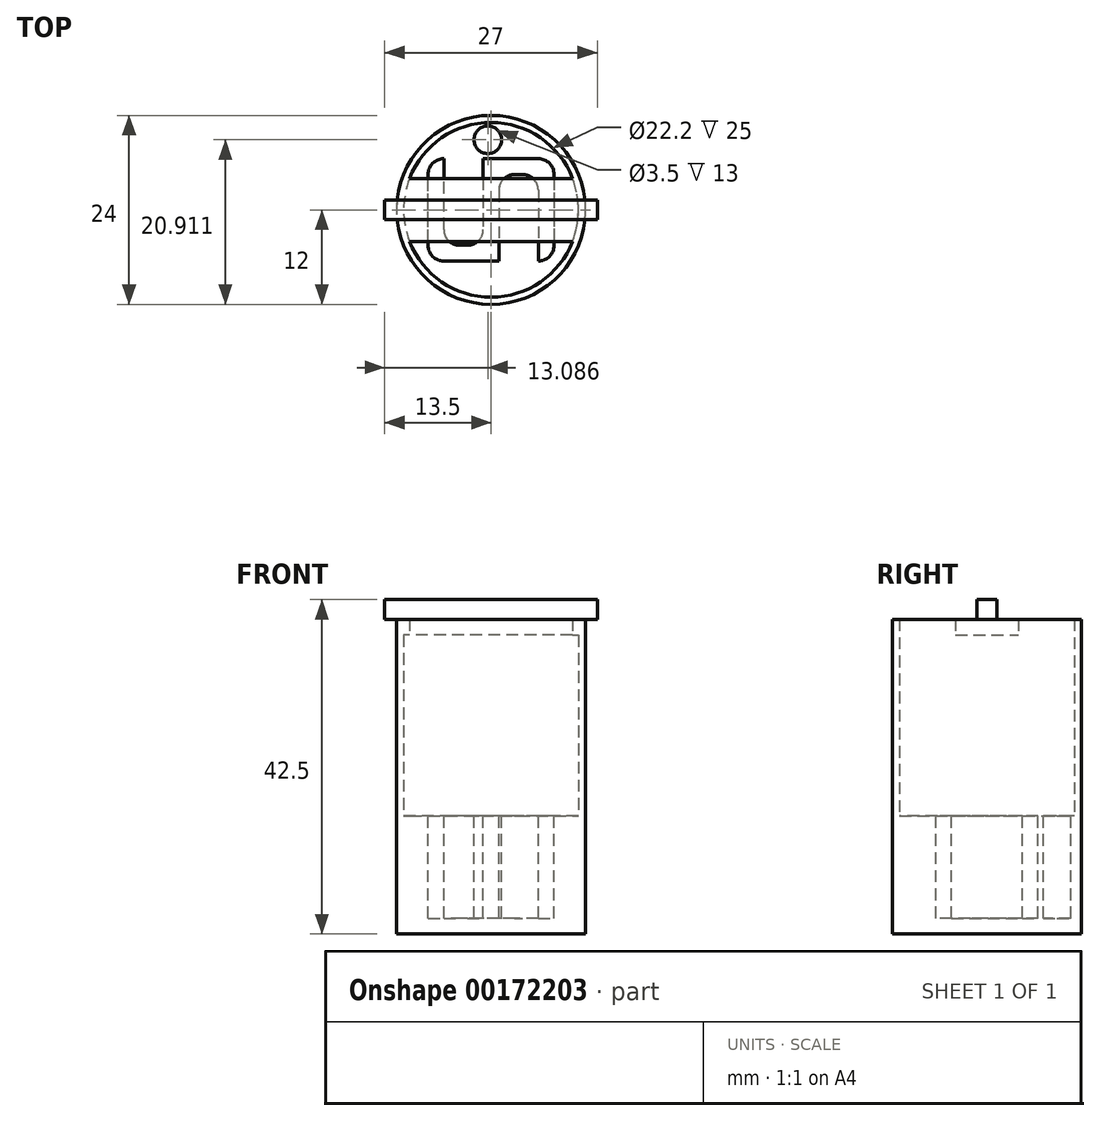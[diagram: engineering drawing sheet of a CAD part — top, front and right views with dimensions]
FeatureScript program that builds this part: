
annotation { "Feature Type Name" : "Feature", "Feature Type Description" : "" }
export const myFeature = defineFeature(function(context is Context, id is Id, definition is map)
    precondition{}
    {
        {
            var Q0;
            Q0=qCreatedBy(makeId("Top.planeOp"),FACE);
            var sketch = newSketch(context, id + "F0", { "sketchPlane" : qUnion([Q0])});
            skCircle(sketch, "E0", {"center": v(0, 0) * mm, "radius": 12 * mm});
            skSolve(sketch);
        }
        {
            var Q0;
            Q0 = qSketchRegion(id + "F0", true);
            extrude(context, id + "F1", {"entities" : qUnion([Q0]), "depth" : 15 * mm});
        }
        {
            var Q0;
            Q0=makeQuery(id+"F1.opExtrude","CAP_FACE",FACE,{"disambiguationData":[OSD([sQuery(id+"F0.wireOp",EDGE,"E0")])],"isStart":false});
            var sketch = newSketch(context, id + "F2", { "sketchPlane" : qUnion([Q0])});
            skLineSegment(sketch, "E1.bottom", {"start": v(1, 6.5) * mm, "end": v(-1, 6.5) * mm});
            skLineSegment(sketch, "E1.top", {"start": v(1, -6.5) * mm, "end": v(-1, -6.5) * mm});
            skLineSegment(sketch, "E1.left", {"start": v(1, 6.5) * mm, "end": v(1, -6.5) * mm});
            skLineSegment(sketch, "E1.right", {"start": v(-1, 6.5) * mm, "end": v(-1, -6.5) * mm});
            skPoint(sketch, "E1.middle", {"position": v(0, 0) * mm});
            skLineSegment(sketch, "E2.bottom", {"start": v(1, -6.5) * mm, "end": v(-8, -6.5) * mm});
            skLineSegment(sketch, "E2.top", {"start": v(1, -4.5) * mm, "end": v(-8, -4.5) * mm});
            skLineSegment(sketch, "E2.left", {"start": v(1, -6.5) * mm, "end": v(1, -4.5) * mm});
            skLineSegment(sketch, "E2.right", {"start": v(-8, -6.5) * mm, "end": v(-8, -4.5) * mm});
            skLineSegment(sketch, "E3.bottom", {"start": v(-8, -6.5) * mm, "end": v(-6, -6.5) * mm});
            skLineSegment(sketch, "E3.top", {"start": v(-8, 6.5) * mm, "end": v(-6, 6.5) * mm});
            skLineSegment(sketch, "E3.left", {"start": v(-8, -6.5) * mm, "end": v(-8, 6.5) * mm});
            skLineSegment(sketch, "E3.right", {"start": v(-6, -6.5) * mm, "end": v(-6, 6.5) * mm});
            skLineSegment(sketch, "E4.bottom", {"start": v(-1, 6.5) * mm, "end": v(8, 6.5) * mm});
            skLineSegment(sketch, "E4.top", {"start": v(-1, 4.5) * mm, "end": v(8, 4.5) * mm});
            skLineSegment(sketch, "E4.left", {"start": v(-1, 6.5) * mm, "end": v(-1, 4.5) * mm});
            skLineSegment(sketch, "E4.right", {"start": v(8, 6.5) * mm, "end": v(8, 4.5) * mm});
            skLineSegment(sketch, "E5.bottom", {"start": v(8, 6.5) * mm, "end": v(6, 6.5) * mm});
            skLineSegment(sketch, "E5.top", {"start": v(8, -6.5) * mm, "end": v(6, -6.5) * mm});
            skLineSegment(sketch, "E5.left", {"start": v(8, 6.5) * mm, "end": v(8, -6.5) * mm});
            skLineSegment(sketch, "E5.right", {"start": v(6, 6.5) * mm, "end": v(6, -6.5) * mm});
            skSolve(sketch);
        }
        {
            var Q0;
            Q0 = qSketchRegion(id + "F2", true);
            extrude(context, id + "F3", {"entities" : qUnion([Q0]), "operationType" : NewBodyOperationType.REMOVE, "oppositeDirection" : true, "depth" : 13 * mm});
        }
        {
            var Q0;
            Q0=makeQuery(id+"F1.opExtrude","CAP_FACE",FACE,{"disambiguationData":[OSD([sQuery(id+"F0.wireOp",EDGE,"E0")])],"isStart":false});
            var sketch = newSketch(context, id + "F4", { "sketchPlane" : qUnion([Q0])});
            skCircle(sketch, "E6", {"center": v(0, 0) * mm, "radius": 12 * mm});
            skCircle(sketch, "E7", {"center": v(0, 0) * mm, "radius": 11.1 * mm});
            skSolve(sketch);
        }
        {
            var Q0;
            Q0 = qSketchRegion(id + "F4", true);
            extrude(context, id + "F5", {"entities" : qUnion([Q0]), "operationType" : NewBodyOperationType.ADD, "depth" : 25 * mm});
        }
        {
            var Q0;
            Q0=makeQuery(id+"F5.opExtrude","CAP_FACE",FACE,{"disambiguationData":[OSD([sQuery(id+"F4.wireOp",EDGE,"E6"),sQuery(id+"F4.wireOp",EDGE,"E7")])],"isStart":false});
            var sketch = newSketch(context, id + "F6", { "sketchPlane" : qUnion([Q0])});
            skLineSegment(sketch, "E8.bottom", {"start": v(14.81, -4) * mm, "end": v(-14.81, -4) * mm});
            skLineSegment(sketch, "E8.top", {"start": v(14.81, 4) * mm, "end": v(-14.81, 4) * mm});
            skLineSegment(sketch, "E8.left", {"start": v(14.81, -4) * mm, "end": v(14.81, 4) * mm});
            skLineSegment(sketch, "E8.right", {"start": v(-14.81, -4) * mm, "end": v(-14.81, 4) * mm});
            skPoint(sketch, "E8.middle", {"position": v(0, 0) * mm});
            skLineSegment(sketch, "E9.bottom", {"start": v(-14.81, 4) * mm, "end": v(15.46, 4) * mm});
            skLineSegment(sketch, "E9.top", {"start": v(-14.81, 13.03) * mm, "end": v(15.46, 13.03) * mm});
            skLineSegment(sketch, "E9.left", {"start": v(-14.81, 4) * mm, "end": v(-14.81, 13.03) * mm});
            skLineSegment(sketch, "E9.right", {"start": v(15.46, 4) * mm, "end": v(15.46, 13.03) * mm});
            skLineSegment(sketch, "E10.bottom", {"start": v(-14.81, -4) * mm, "end": v(14.97, -4) * mm});
            skLineSegment(sketch, "E10.top", {"start": v(-14.81, -14.85) * mm, "end": v(14.97, -14.85) * mm});
            skLineSegment(sketch, "E10.left", {"start": v(-14.81, -4) * mm, "end": v(-14.81, -14.85) * mm});
            skLineSegment(sketch, "E10.right", {"start": v(14.97, -4) * mm, "end": v(14.97, -14.85) * mm});
            skSolve(sketch);
        }
        {
            var Q0;
            {var subQ0=sQuery(id+"F6.wireOp",EDGE,"E9.bottom");var subQ1=makeQuery(id+"F5.opExtrude","CAP_EDGE",EDGE,{"disambiguationData":[OSD([sQuery(id+"F4.wireOp",EDGE,"E7")])],"isStart":false});var subQ2=makeQuery(id+"F6.imprint","INTERSECT",VERTEX,{"disambiguationData":[OD(0.0)],"derivedFrom":[subQ1,subQ0]});Q0=makeQuery(id+"F6.imprint","IMPRINT",FACE,{"disambiguationData":[TD([[makeQuery(id+"F6.imprint","IMPRINT",EDGE,{"disambiguationData":[TD([[subQ2,-1.0]])],"derivedFrom":subQ0}),1.0]])]});}
            var Q1;
            {var subQ0=sQuery(id+"F6.wireOp",EDGE,"E10.bottom");var subQ1=makeQuery(id+"F5.opExtrude","CAP_EDGE",EDGE,{"disambiguationData":[OSD([sQuery(id+"F4.wireOp",EDGE,"E7")])],"isStart":false});var subQ2=makeQuery(id+"F6.imprint","INTERSECT",VERTEX,{"disambiguationData":[OD(0.0)],"derivedFrom":[subQ1,subQ0]});Q1=makeQuery(id+"F6.imprint","IMPRINT",FACE,{"disambiguationData":[TD([[makeQuery(id+"F6.imprint","IMPRINT",EDGE,{"disambiguationData":[TD([[subQ2,-1.0]])],"derivedFrom":subQ0}),-1.0]])]});}
            var Q2;
            Q2=makeQuery(id+"F6.imprint","IMPRINT",FACE,{"disambiguationData":[TD([[makeQuery(id+"F6.imprint","IMPRINT",EDGE,{"derivedFrom":sQuery(id+"F6.wireOp",EDGE,"E9.top")}),-1.0]])]});
            var Q3;
            Q3=makeQuery(id+"F6.imprint","IMPRINT",FACE,{"disambiguationData":[TD([[makeQuery(id+"F6.imprint","IMPRINT",EDGE,{"derivedFrom":sQuery(id+"F6.wireOp",EDGE,"E10.top")}),1.0]])]});
            var Q4;
            {var subQ0=sQuery(id+"F6.wireOp",EDGE,"E9.bottom");var subQ1=makeQuery(id+"F5.opExtrude","CAP_EDGE",EDGE,{"disambiguationData":[OSD([sQuery(id+"F4.wireOp",EDGE,"E6")])],"isStart":false});var subQ2=makeQuery(id+"F6.imprint","INTERSECT",VERTEX,{"disambiguationData":[OD(0.0)],"derivedFrom":[subQ1,subQ0]});Q4=makeQuery(id+"F6.imprint","IMPRINT",FACE,{"disambiguationData":[TD([[makeQuery(id+"F6.imprint","IMPRINT",EDGE,{"disambiguationData":[TD([[subQ2,-1.0]])],"derivedFrom":subQ0}),1.0]])]});}
            var Q5;
            {var subQ0=sQuery(id+"F6.wireOp",EDGE,"E10.bottom");var subQ1=makeQuery(id+"F5.opExtrude","CAP_EDGE",EDGE,{"disambiguationData":[OSD([sQuery(id+"F4.wireOp",EDGE,"E6")])],"isStart":false});var subQ2=makeQuery(id+"F6.imprint","INTERSECT",VERTEX,{"disambiguationData":[OD(0.0)],"derivedFrom":[subQ1,subQ0]});Q5=makeQuery(id+"F6.imprint","IMPRINT",FACE,{"disambiguationData":[TD([[makeQuery(id+"F6.imprint","IMPRINT",EDGE,{"disambiguationData":[TD([[subQ2,-1.0]])],"derivedFrom":subQ0}),-1.0]])]});}
            extrude(context, id + "F7", {"entities" : qUnion([Q0, Q1, Q2, Q3, Q4, Q5]), "operationType" : NewBodyOperationType.REMOVE, "oppositeDirection" : true, "depth" : 25 * mm});
        }
        {
            var Q0;
            Q0=makeQuery(id+"F7.boolean.opBoolean","SPLIT",FACE,{"disambiguationData":[OD(1.0)],"derivedFrom":makeQuery(id+"F5.opExtrude","CAP_FACE",FACE,{"disambiguationData":[OSD([sQuery(id+"F4.wireOp",EDGE,"E6"),sQuery(id+"F4.wireOp",EDGE,"E7")])],"isStart":false})});
            var sketch = newSketch(context, id + "F8", { "sketchPlane" : qUnion([Q0])});
            skLineSegment(sketch, "E11.bottom", {"start": v(11.31, 4) * mm, "end": v(-11.31, 4) * mm});
            skLineSegment(sketch, "E11.top", {"start": v(11.31, -4) * mm, "end": v(-11.31, -4) * mm});
            skLineSegment(sketch, "E11.left", {"start": v(11.31, 4) * mm, "end": v(11.31, -4) * mm});
            skLineSegment(sketch, "E11.right", {"start": v(-11.31, 4) * mm, "end": v(-11.31, -4) * mm});
            skPoint(sketch, "E11.middle", {"position": v(0, 0) * mm});
            skSolve(sketch);
        }
        {
            var Q0;
            Q0 = qSketchRegion(id + "F8", true);
            extrude(context, id + "F9", {"entities" : qUnion([Q0]), "operationType" : NewBodyOperationType.ADD, "oppositeDirection" : true, "depth" : 2 * mm});
        }
        {
            var Q0;
            {var subQ0=makeQuery(id+"F5.opExtrude","CAP_FACE",FACE,{"disambiguationData":[OSD([sQuery(id+"F4.wireOp",EDGE,"E6"),sQuery(id+"F4.wireOp",EDGE,"E7")])],"isStart":false});Q0=makeQuery(id+"F9.boolean.opBoolean","MERGE",FACE,{"derivedFrom":[makeQuery(id+"F7.boolean.opBoolean","SPLIT",FACE,{"disambiguationData":[OD(0.0)],"derivedFrom":subQ0}),makeQuery(id+"F7.boolean.opBoolean","SPLIT",FACE,{"disambiguationData":[OD(1.0)],"derivedFrom":subQ0}),makeQuery(id+"F9.opExtrude","CAP_FACE",FACE,{"disambiguationData":[OSD([sQuery(id+"F8.wireOp",EDGE,"E11.bottom"),sQuery(id+"F8.wireOp",EDGE,"E11.top"),sQuery(id+"F8.wireOp",EDGE,"E11.left"),sQuery(id+"F8.wireOp",EDGE,"E11.right")])],"isStart":true})]});}
            var sketch = newSketch(context, id + "F10", { "sketchPlane" : qUnion([Q0])});
            skLineSegment(sketch, "E12.bottom", {"start": v(13.5, -1.25) * mm, "end": v(-13.5, -1.25) * mm});
            skLineSegment(sketch, "E12.top", {"start": v(13.5, 1.25) * mm, "end": v(-13.5, 1.25) * mm});
            skLineSegment(sketch, "E12.left", {"start": v(13.5, -1.25) * mm, "end": v(13.5, 1.25) * mm});
            skLineSegment(sketch, "E12.right", {"start": v(-13.5, -1.25) * mm, "end": v(-13.5, 1.25) * mm});
            skPoint(sketch, "E12.middle", {"position": v(0, 0) * mm});
            skSolve(sketch);
        }
        {
            var Q0;
            Q0 = qSketchRegion(id + "F10", true);
            extrude(context, id + "F11", {"entities" : qUnion([Q0]), "operationType" : NewBodyOperationType.ADD, "depth" : 2.5 * mm});
        }
        {
            var Q0;
            Q0=makeQuery(id+"F3.boolean.opBoolean","COPY",EDGE,{"derivedFrom":makeQuery(id+"F3.opExtrude","SWEPT_EDGE",EDGE,{"disambiguationData":[OSD([sQuery(id+"F2.wireOp",EDGE,"E1.right"),sQuery(id+"F2.wireOp",EDGE,"E2.top")])]})});
            var Q1;
            Q1=makeQuery(id+"F3.boolean.opBoolean","COPY",EDGE,{"derivedFrom":makeQuery(id+"F3.opExtrude","SWEPT_EDGE",EDGE,{"disambiguationData":[OSD([sQuery(id+"F2.wireOp",EDGE,"E2.top"),sQuery(id+"F2.wireOp",EDGE,"E3.right")])]})});
            var Q2;
            Q2=makeQuery(id+"F3.boolean.opBoolean","COPY",EDGE,{"derivedFrom":makeQuery(id+"F3.opExtrude","SWEPT_EDGE",EDGE,{"disambiguationData":[OSD([sQuery(id+"F2.wireOp",EDGE,"E4.top"),sQuery(id+"F2.wireOp",EDGE,"E5.right")])]})});
            var Q3;
            Q3=makeQuery(id+"F3.boolean.opBoolean","COPY",EDGE,{"derivedFrom":makeQuery(id+"F3.opExtrude","SWEPT_EDGE",EDGE,{"disambiguationData":[OSD([sQuery(id+"F2.wireOp",EDGE,"E1.left"),sQuery(id+"F2.wireOp",EDGE,"E4.top")])]})});
            fillet(context, id + "F12", {"entities" : qUnion([Q0, Q1, Q2, Q3]), "radius" : 2 * mm, "tangentPropagation" : true, "allowEdgeOverflow" : false});
        }
        {
            var Q0;
            Q0=makeQuery(id+"F3.boolean.opBoolean","COPY",EDGE,{"derivedFrom":makeQuery(id+"F3.opExtrude","SWEPT_EDGE",EDGE,{"disambiguationData":[OSD([sQuery(id+"F2.wireOp",EDGE,"E3.top"),sQuery(id+"F2.wireOp",EDGE,"E3.left")])]})});
            var Q1;
            Q1=makeQuery(id+"F3.boolean.opBoolean","COPY",EDGE,{"derivedFrom":makeQuery(id+"F3.opExtrude","SWEPT_EDGE",EDGE,{"disambiguationData":[OSD([sQuery(id+"F2.wireOp",EDGE,"E4.bottom"),sQuery(id+"F2.wireOp",EDGE,"E4.left")])]})});
            var Q2;
            Q2=makeQuery(id+"F3.boolean.opBoolean","COPY",EDGE,{"derivedFrom":makeQuery(id+"F3.opExtrude","SWEPT_EDGE",EDGE,{"disambiguationData":[OSD([sQuery(id+"F2.wireOp",EDGE,"E5.bottom"),sQuery(id+"F2.wireOp",EDGE,"E5.left")])]})});
            var Q3;
            Q3=makeQuery(id+"F3.boolean.opBoolean","COPY",EDGE,{"derivedFrom":makeQuery(id+"F3.opExtrude","SWEPT_EDGE",EDGE,{"disambiguationData":[OSD([sQuery(id+"F2.wireOp",EDGE,"E3.bottom"),sQuery(id+"F2.wireOp",EDGE,"E3.left")])]})});
            var Q4;
            Q4=makeQuery(id+"F3.boolean.opBoolean","COPY",EDGE,{"derivedFrom":makeQuery(id+"F3.opExtrude","SWEPT_EDGE",EDGE,{"disambiguationData":[OSD([sQuery(id+"F2.wireOp",EDGE,"E2.bottom"),sQuery(id+"F2.wireOp",EDGE,"E2.left")])]})});
            var Q5;
            Q5=makeQuery(id+"F3.boolean.opBoolean","COPY",EDGE,{"derivedFrom":makeQuery(id+"F3.opExtrude","SWEPT_EDGE",EDGE,{"disambiguationData":[OSD([sQuery(id+"F2.wireOp",EDGE,"E5.top"),sQuery(id+"F2.wireOp",EDGE,"E5.left")])]})});
            fillet(context, id + "F13", {"entities" : qUnion([Q0, Q1, Q2, Q3, Q4, Q5]), "radius" : 2 * mm, "tangentPropagation" : true, "allowEdgeOverflow" : false});
        }
        {
            var Q0;
            Q0=makeQuery(id+"F7.boolean.opBoolean","MERGE",FACE,{"derivedFrom":[makeQuery(id+"F1.opExtrude","CAP_FACE",FACE,{"disambiguationData":[OSD([sQuery(id+"F0.wireOp",EDGE,"E0")])],"isStart":false}),makeQuery(id+"F7.opExtrude","CAP_FACE",FACE,{"disambiguationData":[OSD([sQuery(id+"F6.wireOp",EDGE,"E9.bottom"),sQuery(id+"F6.wireOp",EDGE,"E9.top"),sQuery(id+"F6.wireOp",EDGE,"E9.left"),sQuery(id+"F6.wireOp",EDGE,"E9.right")])],"isStart":false}),makeQuery(id+"F7.opExtrude","CAP_FACE",FACE,{"disambiguationData":[OSD([sQuery(id+"F6.wireOp",EDGE,"E10.bottom"),sQuery(id+"F6.wireOp",EDGE,"E10.top"),sQuery(id+"F6.wireOp",EDGE,"E10.left"),sQuery(id+"F6.wireOp",EDGE,"E10.right")])],"isStart":false})]});
            var sketch = newSketch(context, id + "F14", { "sketchPlane" : qUnion([Q0])});
            skCircle(sketch, "E13", {"center": v(-0.41, 8.91) * mm, "radius": 1.75 * mm});
            skPoint(sketch, "E13.centerSnap0", {"position": v(-0.41, 5.91) * mm});
            skSolve(sketch);
        }
        {
            var Q0;
            Q0 = qSketchRegion(id + "F14", true);
            extrude(context, id + "F15", {"entities" : qUnion([Q0]), "operationType" : NewBodyOperationType.REMOVE, "oppositeDirection" : true, "depth" : 13 * mm});
        }
    });
